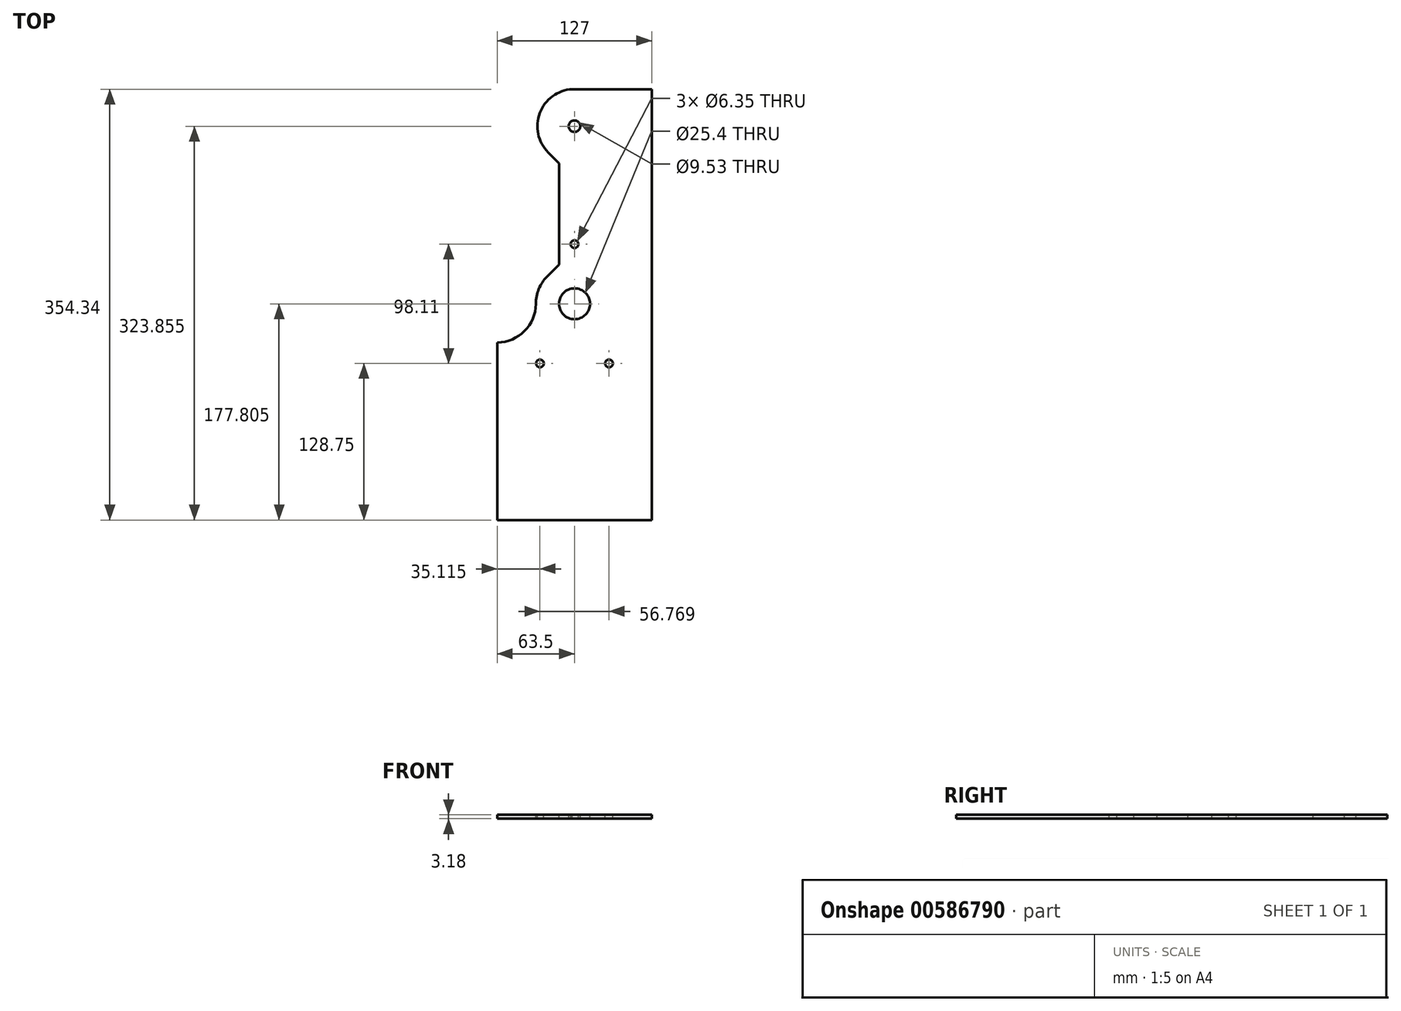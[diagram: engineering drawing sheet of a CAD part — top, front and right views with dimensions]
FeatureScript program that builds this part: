
annotation { "Feature Type Name" : "Feature", "Feature Type Description" : "" }
export const myFeature = defineFeature(function(context is Context, id is Id, definition is map)
    precondition{}
    {
        {
            var Q0;
            Q0=qCreatedBy(makeId("Top.planeOp"),FACE);
            var sketch = newSketch(context, id + "F0", { "sketchPlane" : qUnion([Q0])});
            skLineSegment(sketch, "E0.bottom", {"start": v(63.5, 126.37) * mm, "end": v(-63.5, 126.37) * mm});
            skLineSegment(sketch, "E0.top", {"start": v(63.5, -126.37) * mm, "end": v(-63.5, -126.37) * mm});
            skLineSegment(sketch, "E0.left", {"start": v(63.5, 126.37) * mm, "end": v(63.5, -126.37) * mm});
            skLineSegment(sketch, "E0.right", {"start": v(-63.5, 126.37) * mm, "end": v(-63.5, -126.37) * mm});
            skPoint(sketch, "E0.middle", {"position": v(0, 0) * mm});
            skSolve(sketch);
        }
        {
            var Q0;
            Q0=makeQuery(id+"F0.imprint","IMPRINT",FACE,{"disambiguationData":[TD([[makeQuery(id+"F0.imprint","IMPRINT",EDGE,{"derivedFrom":sQuery(id+"F0.wireOp",EDGE,"E0.bottom")}),1.0]])]});
            extrude(context, id + "F1", {"entities" : qUnion([Q0]), "depth" : 3.17 * mm, "offsetDistance" : 25.4 * mm});
        }
        {
            var Q0;
            Q0=makeQuery(id+"F1.opExtrude","CAP_FACE",FACE,{"disambiguationData":[OSD([sQuery(id+"F0.wireOp",EDGE,"E0.bottom"),sQuery(id+"F0.wireOp",EDGE,"E0.top"),sQuery(id+"F0.wireOp",EDGE,"E0.left"),sQuery(id+"F0.wireOp",EDGE,"E0.right")])],"isStart":false});
            var sketch = newSketch(context, id + "F2", { "sketchPlane" : qUnion([Q0])});
            skLineSegment(sketch, "E1", {"start": v(-21.59, 74.3) * mm, "end": v(-12.7, 65.4) * mm});
            skLineSegment(sketch, "E2", {"start": v(-12.7, 65.4) * mm, "end": v(-12.7, -17.96) * mm});
            skLineSegment(sketch, "E3", {"start": v(-12.7, -17.96) * mm, "end": v(-22.45, -27.71) * mm});
            skLineSegment(sketch, "E4", {"start": v(-63.5, -69.22) * mm, "end": v(-63.5, 116.2) * mm});
            skLineSegment(sketch, "E5", {"start": v(-28.38, -99.22) * mm, "end": v(0, -99.22) * mm, "construction": true});
            skLineSegment(sketch, "E6", {"start": v(0, -99.22) * mm, "end": v(28.38, -99.22) * mm, "construction": true});
            skLineSegment(sketch, "E7", {"start": v(0, -99.22) * mm, "end": v(0, -50.16) * mm, "construction": true});
            skLineSegment(sketch, "E8", {"start": v(0, -50.16) * mm, "end": v(0, -1.11) * mm, "construction": true});
            skCircle(sketch, "E9", {"center": v(0, -50.16) * mm, "radius": 12.7 * mm});
            skCircle(sketch, "E10", {"center": v(28.38, -99.22) * mm, "radius": 3.18 * mm});
            skCircle(sketch, "E11", {"center": v(0, -1.11) * mm, "radius": 3.18 * mm});
            skCircle(sketch, "E12", {"center": v(-28.38, -99.22) * mm, "radius": 3.18 * mm});
            skLineSegment(sketch, "E13", {"start": v(0, -1.11) * mm, "end": v(0, 95.89) * mm, "construction": true});
            skCircle(sketch, "E14", {"center": v(0, 95.89) * mm, "radius": 4.76 * mm});
            skArc(sketch, "E15", {"start": v(-1.8, 126.37) * mm, "mid": v(-28.54, 106.73) * mm, "end": v(-21.59, 74.3) * mm});
            skLineSegment(sketch, "E16", {"start": v(0, 126.37) * mm, "end": v(-63.5, 126.37) * mm});
            skLineSegment(sketch, "E17", {"start": v(-63.5, 126.37) * mm, "end": v(-63.5, 116.2) * mm});
            skArc(sketch, "E18", {"start": v(-22.45, -27.71) * mm, "mid": v(-29.33, -38.01) * mm, "end": v(-31.75, -50.16) * mm});
            skLineSegment(sketch, "E19", {"start": v(0, -50.16) * mm, "end": v(-63.5, -50.16) * mm, "construction": true});
            skArc(sketch, "E20", {"start": v(-31.75, -50.16) * mm, "mid": v(-41.05, -72.62) * mm, "end": v(-63.5, -81.92) * mm});
            skLineSegment(sketch, "E21", {"start": v(-63.5, -69.22) * mm, "end": v(-63.5, -81.92) * mm});
            skSolve(sketch);
        }
        {
            var Q0;
            Q0=makeQuery(id+"F2.imprint","IMPRINT",FACE,{"disambiguationData":[TD([[makeQuery(id+"F2.imprint","IMPRINT",EDGE,{"derivedFrom":sQuery(id+"F2.wireOp",EDGE,"E1")}),-1.0]])]});
            var Q1;
            Q1=makeQuery(id+"F2.imprint","IMPRINT",FACE,{"disambiguationData":[TD([[makeQuery(id+"F2.imprint","IMPRINT",EDGE,{"derivedFrom":sQuery(id+"F2.wireOp",EDGE,"E9")}),1.0]])]});
            var Q2;
            Q2=makeQuery(id+"F2.imprint","IMPRINT",FACE,{"disambiguationData":[TD([[makeQuery(id+"F2.imprint","IMPRINT",EDGE,{"derivedFrom":sQuery(id+"F2.wireOp",EDGE,"E10")}),1.0]])]});
            var Q3;
            Q3=makeQuery(id+"F2.imprint","IMPRINT",FACE,{"disambiguationData":[TD([[makeQuery(id+"F2.imprint","IMPRINT",EDGE,{"derivedFrom":sQuery(id+"F2.wireOp",EDGE,"E12")}),1.0]])]});
            var Q4;
            Q4=makeQuery(id+"F2.imprint","IMPRINT",FACE,{"disambiguationData":[TD([[makeQuery(id+"F2.imprint","IMPRINT",EDGE,{"derivedFrom":sQuery(id+"F2.wireOp",EDGE,"E11")}),1.0]])]});
            var Q5;
            Q5=makeQuery(id+"F2.imprint","IMPRINT",FACE,{"disambiguationData":[TD([[makeQuery(id+"F2.imprint","IMPRINT",EDGE,{"derivedFrom":sQuery(id+"F2.wireOp",EDGE,"E14")}),1.0]])]});
            extrude(context, id + "F3", {"entities" : qUnion([Q0, Q1, Q2, Q3, Q4, Q5]), "operationType" : NewBodyOperationType.REMOVE, "endBound" : BoundingType.THROUGH_ALL, "oppositeDirection" : true, "depth" : 25.4 * mm, "offsetDistance" : 25.4 * mm});
        }
        {
            var Q0;
            Q0=makeQuery(id+"F1.opExtrude","SWEPT_FACE",FACE,{"disambiguationData":[OSD([sQuery(id+"F0.wireOp",EDGE,"E0.top")])]});
            var sketch = newSketch(context, id + "F4", { "sketchPlane" : qUnion([Q0])});
            skLineSegment(sketch, "E22.bottom", {"start": v(63.5, 0) * mm, "end": v(-63.5, 0) * mm});
            skLineSegment(sketch, "E22.top", {"start": v(63.5, 3.18) * mm, "end": v(-63.5, 3.18) * mm});
            skLineSegment(sketch, "E22.left", {"start": v(63.5, 0) * mm, "end": v(63.5, 3.18) * mm});
            skLineSegment(sketch, "E22.right", {"start": v(-63.5, 0) * mm, "end": v(-63.5, 3.18) * mm});
            skSolve(sketch);
        }
        {
            var Q0;
            Q0 = qSketchRegion(id + "F4", true);
            extrude(context, id + "F5", {"entities" : qUnion([Q0]), "operationType" : NewBodyOperationType.ADD, "depth" : 101.6 * mm, "offsetDistance" : 25.4 * mm});
        }
    });
